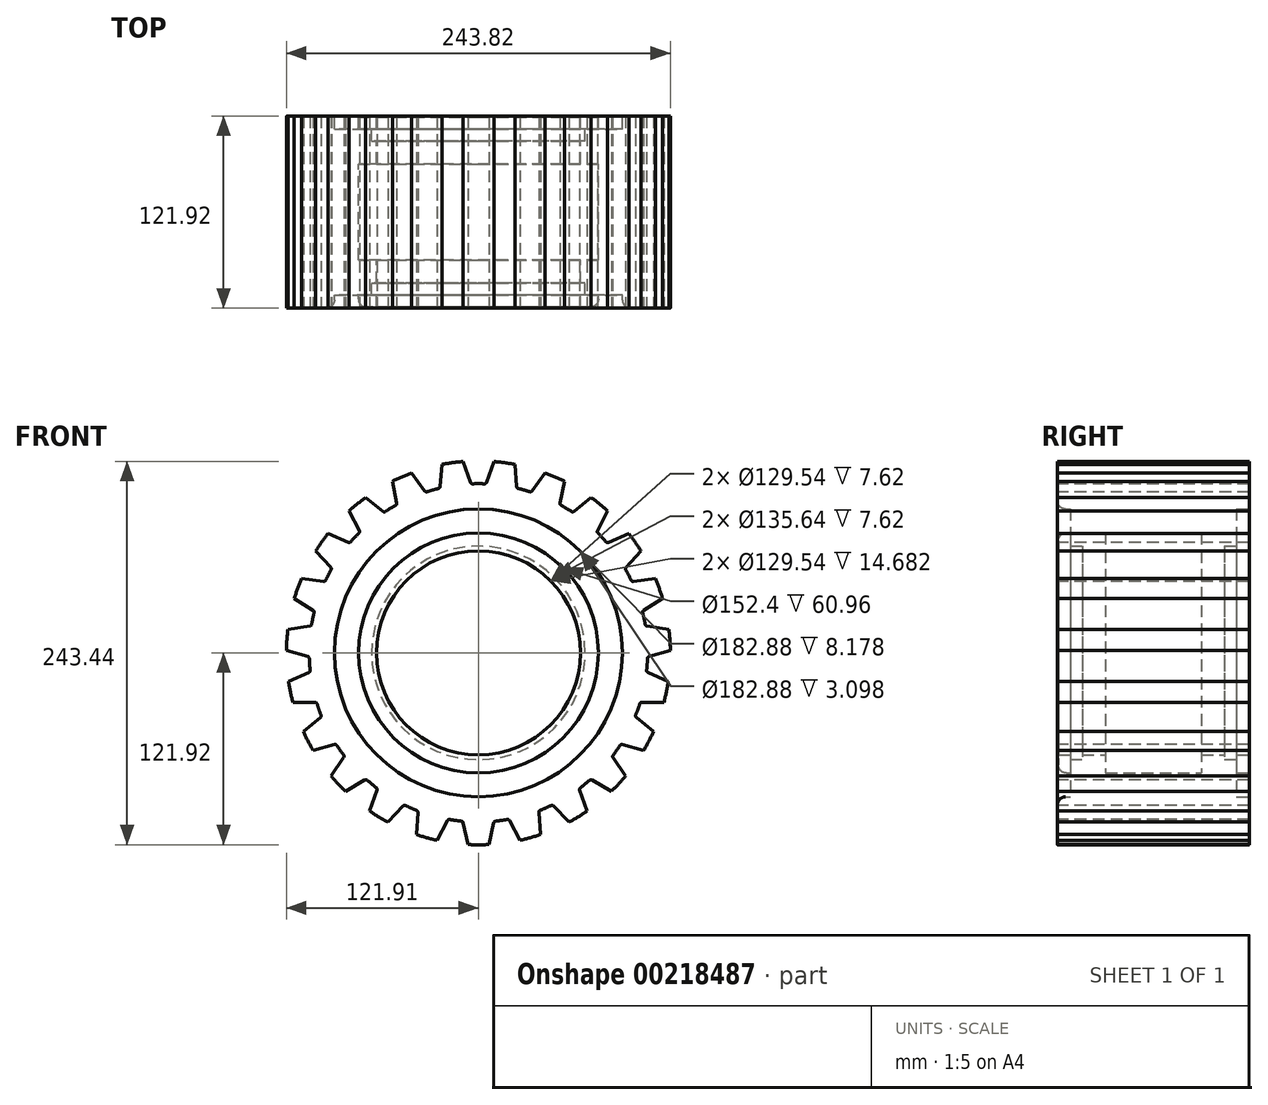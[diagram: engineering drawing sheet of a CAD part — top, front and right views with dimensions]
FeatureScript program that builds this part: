
annotation { "Feature Type Name" : "Feature", "Feature Type Description" : "" }
export const myFeature = defineFeature(function(context is Context, id is Id, definition is map)
    precondition{}
    {
        {
            var Q0;
            Q0=qCreatedBy(makeId("Right.planeOp"),FACE);
            var sketch = newSketch(context, id + "F0", { "sketchPlane" : qUnion([Q0])});
            skLineSegment(sketch, "E0", {"start": v(0, 76.2) * mm, "end": v(-30.48, 76.2) * mm});
            skLineSegment(sketch, "E1", {"start": v(-30.48, 64.77) * mm, "end": v(-30.48, 76.2) * mm});
            skLineSegment(sketch, "E2", {"start": v(-30.48, 64.77) * mm, "end": v(-45.16, 64.77) * mm});
            skLineSegment(sketch, "E3", {"start": v(-45.16, 64.77) * mm, "end": v(-45.16, 67.82) * mm});
            skLineSegment(sketch, "E4", {"start": v(-45.16, 67.82) * mm, "end": v(-52.78, 67.82) * mm});
            skLineSegment(sketch, "E5", {"start": v(-52.78, 67.82) * mm, "end": v(-52.78, 64.77) * mm});
            skLineSegment(sketch, "E6", {"start": v(-52.78, 64.77) * mm, "end": v(-60.4, 64.77) * mm});
            skLineSegment(sketch, "E7", {"start": v(-60.4, 64.77) * mm, "end": v(-60.4, 76.2) * mm});
            skLineSegment(sketch, "E8", {"start": v(-60.4, 76.2) * mm, "end": v(-52.78, 76.2) * mm});
            skLineSegment(sketch, "E9", {"start": v(-52.78, 76.2) * mm, "end": v(-52.78, 91.44) * mm});
            skLineSegment(sketch, "E10", {"start": v(-52.78, 91.44) * mm, "end": v(-60.96, 91.44) * mm});
            skLineSegment(sketch, "E11", {"start": v(-60.96, 91.44) * mm, "end": v(-60.96, 121.92) * mm});
            skLineSegment(sketch, "E12", {"start": v(-60.96, 121.92) * mm, "end": v(0, 121.92) * mm});
            skLineSegment(sketch, "E13.MirrorCS", {"start": v(60.4, 76.2) * mm, "end": v(52.78, 76.2) * mm});
            skLineSegment(sketch, "E14.MirrorCS", {"start": v(45.16, 64.77) * mm, "end": v(45.16, 67.82) * mm});
            skLineSegment(sketch, "E15.MirrorCS", {"start": v(52.78, 64.77) * mm, "end": v(60.4, 64.77) * mm});
            skLineSegment(sketch, "E16.MirrorCS", {"start": v(45.16, 67.82) * mm, "end": v(52.78, 67.82) * mm});
            skLineSegment(sketch, "E17.MirrorCS", {"start": v(52.78, 67.82) * mm, "end": v(52.78, 64.77) * mm});
            skLineSegment(sketch, "E18.MirrorCS", {"start": v(52.78, 91.44) * mm, "end": v(60.96, 91.44) * mm});
            skLineSegment(sketch, "E19.MirrorCS", {"start": v(30.48, 64.77) * mm, "end": v(30.48, 76.2) * mm});
            skLineSegment(sketch, "E20.MirrorCS", {"start": v(60.96, 121.92) * mm, "end": v(0, 121.92) * mm});
            skLineSegment(sketch, "E21.MirrorCS", {"start": v(52.78, 76.2) * mm, "end": v(52.78, 91.44) * mm});
            skLineSegment(sketch, "E22.MirrorCS", {"start": v(30.48, 64.77) * mm, "end": v(45.16, 64.77) * mm});
            skLineSegment(sketch, "E23.MirrorCS", {"start": v(60.4, 64.77) * mm, "end": v(60.4, 76.2) * mm});
            skLineSegment(sketch, "E24.MirrorCS", {"start": v(60.96, 91.44) * mm, "end": v(60.96, 121.92) * mm});
            skLineSegment(sketch, "E25.MirrorCS", {"start": v(0, 76.2) * mm, "end": v(30.48, 76.2) * mm});
            skLineSegment(sketch, "E26", {"start": v(0, 0) * mm, "end": v(-25.63, 0) * mm, "construction": true});
            skSolve(sketch);
        }
        {
            var Q0;
            Q0 = qSketchRegion(id + "F0", true);
            var Q1;
            Q1=sQuery(id+"F0.wireOp",EDGE,"E26");
            revolve(context, id + "F1", {"entities" : qUnion([Q0]), "axis" : qUnion([Q1]), "revolveType" : RevolveType.FULL});
        }
        {
            var Q0;
            Q0=qCreatedBy(makeId("Front.planeOp"),FACE);
            var sketch = newSketch(context, id + "F2", { "sketchPlane" : qUnion([Q0])});
            skArc(sketch, "E27.0", {"start": v(3.84, 107.37) * mm, "mid": v(0, 107.44) * mm, "end": v(-3.84, 107.37) * mm});
            skLineSegment(sketch, "E28", {"start": v(0, 0) * mm, "end": v(0, 123.07) * mm, "construction": true});
            skArc(sketch, "E29.0", {"start": v(9.92, 121.52) * mm, "mid": v(0, 121.92) * mm, "end": v(-9.92, 121.52) * mm});
            skLineSegment(sketch, "E30", {"start": v(5.07, 108.2) * mm, "end": v(9.92, 121.52) * mm});
            skLineSegment(sketch, "E31.MirrorCS", {"start": v(-5.07, 108.2) * mm, "end": v(-9.92, 121.52) * mm});
            skPoint(sketch, "E32.visualSharp", {"position": v(-4.76, 107.34) * mm});
            skArc(sketch, "E32.filletArc", {"start": v(-5.07, 108.2) * mm, "mid": v(-4.6, 107.59) * mm, "end": v(-3.84, 107.37) * mm});
            skPoint(sketch, "E33.visualSharp", {"position": v(4.76, 107.34) * mm});
            skArc(sketch, "E33.filletArc", {"start": v(3.84, 107.37) * mm, "mid": v(4.6, 107.59) * mm, "end": v(5.07, 108.2) * mm});
            skSolve(sketch);
        }
        {
            var Q0;
            Q0 = qSketchRegion(id + "F2", true);
            extrude(context, id + "F3", {"entities" : qUnion([Q0]), "operationType" : NewBodyOperationType.REMOVE, "endBound" : BoundingType.SYMMETRIC, "oppositeDirection" : true, "depth" : 127 * mm});
        }
        {
            var Q0;
            Q0=makeQuery(id+"F1.opRevolve","SWEPT_BODY",BODY,{"disambiguationData":[OSD([sQuery(id+"F0.wireOp",EDGE,"E0"),sQuery(id+"F0.wireOp",EDGE,"E1"),sQuery(id+"F0.wireOp",EDGE,"E2"),sQuery(id+"F0.wireOp",EDGE,"E3"),sQuery(id+"F0.wireOp",EDGE,"E4"),sQuery(id+"F0.wireOp",EDGE,"E5"),sQuery(id+"F0.wireOp",EDGE,"E6"),sQuery(id+"F0.wireOp",EDGE,"E7"),sQuery(id+"F0.wireOp",EDGE,"E8"),sQuery(id+"F0.wireOp",EDGE,"E9"),sQuery(id+"F0.wireOp",EDGE,"E10"),sQuery(id+"F0.wireOp",EDGE,"E11"),sQuery(id+"F0.wireOp",EDGE,"E12"),sQuery(id+"F0.wireOp",EDGE,"E13.MirrorCS"),sQuery(id+"F0.wireOp",EDGE,"E14.MirrorCS"),sQuery(id+"F0.wireOp",EDGE,"E15.MirrorCS"),sQuery(id+"F0.wireOp",EDGE,"E16.MirrorCS"),sQuery(id+"F0.wireOp",EDGE,"E17.MirrorCS"),sQuery(id+"F0.wireOp",EDGE,"E18.MirrorCS"),sQuery(id+"F0.wireOp",EDGE,"E19.MirrorCS"),sQuery(id+"F0.wireOp",EDGE,"E20.MirrorCS"),sQuery(id+"F0.wireOp",EDGE,"E21.MirrorCS"),sQuery(id+"F0.wireOp",EDGE,"E22.MirrorCS"),sQuery(id+"F0.wireOp",EDGE,"E23.MirrorCS"),sQuery(id+"F0.wireOp",EDGE,"E24.MirrorCS"),sQuery(id+"F0.wireOp",EDGE,"E25.MirrorCS")])]});
            var Q1;
            Q1=makeQuery(id+"F3.boolean.opBoolean","COPY",FACE,{"derivedFrom":makeQuery(id+"F3.opExtrude","SWEPT_FACE",FACE,{"disambiguationData":[OSD([sQuery(id+"F2.wireOp",EDGE,"E31.MirrorCS")])]})});
            var Q2;
            Q2=makeQuery(id+"F3.boolean.opBoolean","COPY",FACE,{"derivedFrom":makeQuery(id+"F3.opExtrude","SWEPT_FACE",FACE,{"disambiguationData":[OSD([sQuery(id+"F2.wireOp",EDGE,"E32.filletArc")])]})});
            var Q3;
            Q3=makeQuery(id+"F3.boolean.opBoolean","COPY",FACE,{"derivedFrom":makeQuery(id+"F3.opExtrude","SWEPT_FACE",FACE,{"disambiguationData":[OSD([sQuery(id+"F2.wireOp",EDGE,"E27.0")])]})});
            var Q4;
            Q4=makeQuery(id+"F3.boolean.opBoolean","COPY",FACE,{"derivedFrom":makeQuery(id+"F3.opExtrude","SWEPT_FACE",FACE,{"disambiguationData":[OSD([sQuery(id+"F2.wireOp",EDGE,"E33.filletArc")])]})});
            var Q5;
            Q5=makeQuery(id+"F3.boolean.opBoolean","COPY",FACE,{"derivedFrom":makeQuery(id+"F3.opExtrude","SWEPT_FACE",FACE,{"disambiguationData":[OSD([sQuery(id+"F2.wireOp",EDGE,"E30")])]})});
            var Q6;
            Q6=makeQuery(id+"F1.opRevolve","SWEPT_FACE",FACE,{"disambiguationData":[OSD([sQuery(id+"F0.wireOp",EDGE,"E0"),sQuery(id+"F0.wireOp",EDGE,"E25.MirrorCS")])]});
            circularPattern(context, id + "F4", {"patternType" : PatternType.FACE, "faces" : qUnion([Q1, Q2, Q3, Q4, Q5]), "axis" : qUnion([Q6]), "angle" : 360 * degree, "instanceCount" : 46, "equalSpace" : true});
        }
        {
            var Q0;
            Q0=makeQuery(id+"F1.opRevolve","SWEPT_EDGE",EDGE,{"disambiguationData":[OSD([sQuery(id+"F0.wireOp",EDGE,"E7"),sQuery(id+"F0.wireOp",EDGE,"E8")])]});
            fillet(context, id + "F5", {"entities" : qUnion([Q0]), "radius" : 5.08 * mm, "tangentPropagation" : true, "allowEdgeOverflow" : false});
        }
        {
            var Q0;
            Q0=makeQuery(id+"F1.opRevolve","SWEPT_EDGE",EDGE,{"disambiguationData":[OSD([sQuery(id+"F0.wireOp",EDGE,"E10"),sQuery(id+"F0.wireOp",EDGE,"E11")])]});
            fillet(context, id + "F6", {"entities" : qUnion([Q0]), "radius" : 5.08 * mm, "tangentPropagation" : true, "allowEdgeOverflow" : false});
        }
    });
